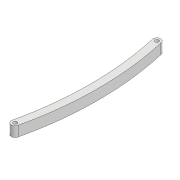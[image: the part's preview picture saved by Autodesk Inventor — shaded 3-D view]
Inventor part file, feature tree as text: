
AUTODESK INVENTOR PART (.ipt)
format: ipt  version: 2022 (Build 260153000, 153)  size: 92,160 bytes
history: native  units: mm
features: extrude x1, sketch x1
ambient origin geometry x8: Origin, YZ Plane, XZ Plane, XY Plane, X Axis, Y Axis, Z Axis, Center Point
bodies: Solid1 (feature_tree)
feature tree (2):
  extrude  "Extrusion1"  Depth=400.0mm
  sketch  "Sketch1"  dims[d0=111.226mm d1=6.0mm d2=3.0mm d3=3.0mm d4=8.0mm d5=0.0mm d10=400.0mm d11=400.0mm]
